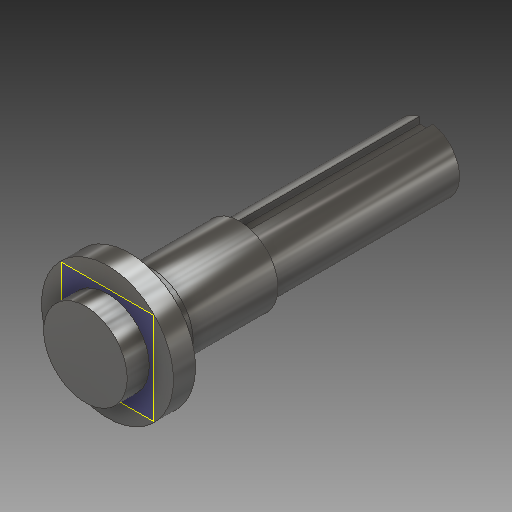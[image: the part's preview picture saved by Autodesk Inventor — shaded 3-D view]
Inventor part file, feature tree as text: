
AUTODESK INVENTOR PART (.ipt)
format: ipt  version: 2019 (Build 230136000, 136)  size: 156,672 bytes
history: native  units: in
note: dims shown in document units (in); Inventor stores cm internally (conversion verified against a paired STEP export)
features: sketch x5, other x3, plane x1
ambient origin geometry x8: Origin, YZ Plane, XZ Plane, XY Plane, X Axis, Y Axis, Z Axis, Center Point
bodies: Solid1 (feature_tree)
feature tree (9):
  other  "project handle part.ipt"
  other  "Solid1::project handle part.ipt"
  other  "TaggingFeature1"
  sketch  "Sketch1"  dims[d0=0.3937in]
  sketch  "Sketch2"
  sketch  "Sketch3"
  sketch  "Sketch4"
  sketch  "Sketch5"
  plane  "Work Plane1"
